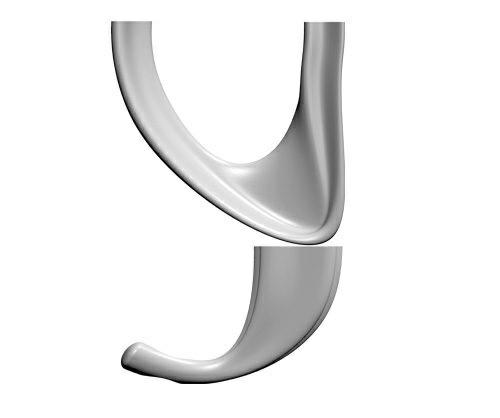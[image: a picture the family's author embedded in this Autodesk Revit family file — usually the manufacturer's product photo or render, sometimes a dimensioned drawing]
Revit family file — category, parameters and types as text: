
# Revit family: CITY ALPHABET letter „Y”
name_source: partatom
category: Furniture
revit_build: Autodesk Revit 2018 (Build: 20190510_1515(x64)
units: mm (PartAtom-declared; Revit-internal decimal feet)

## family parameters
Cut with Voids When Loaded = No
Host = Face
OmniClass Number = 23.40.10.11.14
OmniClass Title = Exterior Seating
Room Calculation Point = No
Shared = No

## types (1)
- CITY ALPHABET letter „Y”
    Default Elevation = 1219 mm
    Height = 850 mm  [stored 2.78871 ft]
    IfcExportAs = IfcFurnishingElement
    Length = 1900 mm  [stored 6.2336 ft]
    Manufacturer = Astrini Design
    Material information = Colour choice from RAL colour standard. Customer may inquire about specific request regarding individual order.
    Model = CITY ALPHABET letter „Y”
    Operating temperature = -40°C to 80°C, ( -40°F to 176°F )
    Type Comments = Bench
    Type Image = Y.jpg
    URL = https://astrini-design.pl
    Weight (approximately) = 106.00 kg
    Weight - filled (approximately) = 206.00 kg
    Width = 2960 mm  [stored 9.71129 ft]

note: [stored X ft] marks values corroborated as IEEE doubles in the binary element streams (Revit-internal decimal feet)
